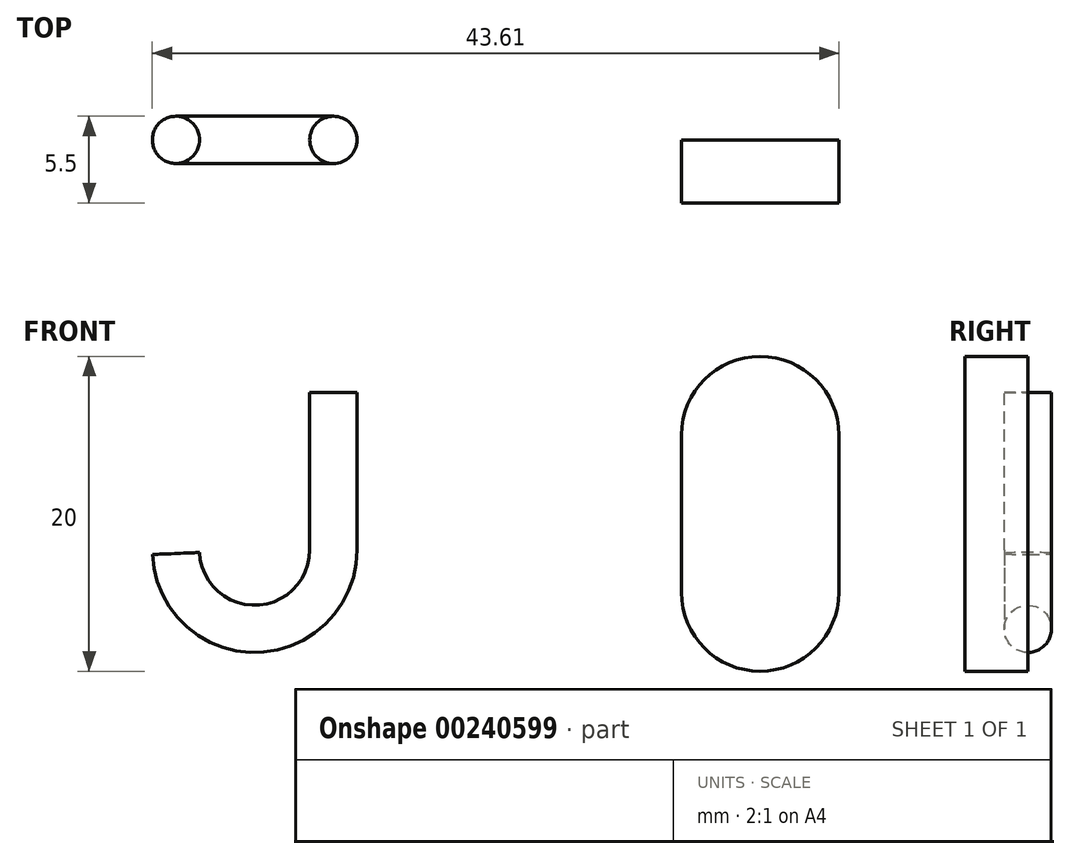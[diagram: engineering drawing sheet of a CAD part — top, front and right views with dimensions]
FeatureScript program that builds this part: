
annotation { "Feature Type Name" : "Feature", "Feature Type Description" : "" }
export const myFeature = defineFeature(function(context is Context, id is Id, definition is map)
    precondition{}
    {
        {
            var Q0;
            Q0=qCreatedBy(makeId("Front.planeOp"),FACE);
            var sketch = newSketch(context, id + "F0", { "sketchPlane" : qUnion([Q0])});
            skLineSegment(sketch, "E0", {"start": v(21.3, 2.7) * mm, "end": v(21.3, -7.3) * mm});
            skArc(sketch, "E1", {"start": v(21.3, -7.3) * mm, "mid": v(16.4, -12.3) * mm, "end": v(11.3, -7.52) * mm});
            skLineSegment(sketch, "E2", {"start": v(43.4, 0) * mm, "end": v(43.4, -10) * mm});
            skLineSegment(sketch, "E3", {"start": v(53.4, 0) * mm, "end": v(53.4, -10) * mm});
            skArc(sketch, "E4", {"start": v(43.4, -10) * mm, "mid": v(48.4, -15) * mm, "end": v(53.4, -10) * mm});
            skArc(sketch, "E5", {"start": v(43.4, 0) * mm, "mid": v(48.4, 5) * mm, "end": v(53.4, 0) * mm});
            skSolve(sketch);
        }
        {
            var Q0;
            Q0=qCreatedBy(makeId("Top.planeOp"),FACE);
            var sketch = newSketch(context, id + "F1", { "sketchPlane" : qUnion([Q0])});
            skCircle(sketch, "E6", {"center": v(21.3, 0) * mm, "radius": 1.5 * mm});
            skSolve(sketch);
        }
        {
            var Q0;
            Q0=makeQuery(id+"F1.imprint","IMPRINT",FACE,{"disambiguationData":[TD([[makeQuery(id+"F1.imprint","IMPRINT",EDGE,{"derivedFrom":sQuery(id+"F1.wireOp",EDGE,"E6")}),1.0]])]});
            var Q1;
            Q1=sQuery(id+"F0.wireOp",EDGE,"E1");
            var Q2;
            Q2=sQuery(id+"F0.wireOp",EDGE,"E0");
            sweep(context, id + "F2", {"profiles" : qUnion([Q0]), "path" : qUnion([Q1, Q2])});
        }
        {
            var Q0;
            Q0=makeQuery(id+"F0.imprint","IMPRINT",FACE,{"disambiguationData":[TD([[makeQuery(id+"F0.imprint","IMPRINT",EDGE,{"derivedFrom":sQuery(id+"F0.wireOp",EDGE,"E2")}),1.0]])]});
            extrude(context, id + "F3", {"entities" : qUnion([Q0]), "depth" : 4 * mm});
        }
    });
